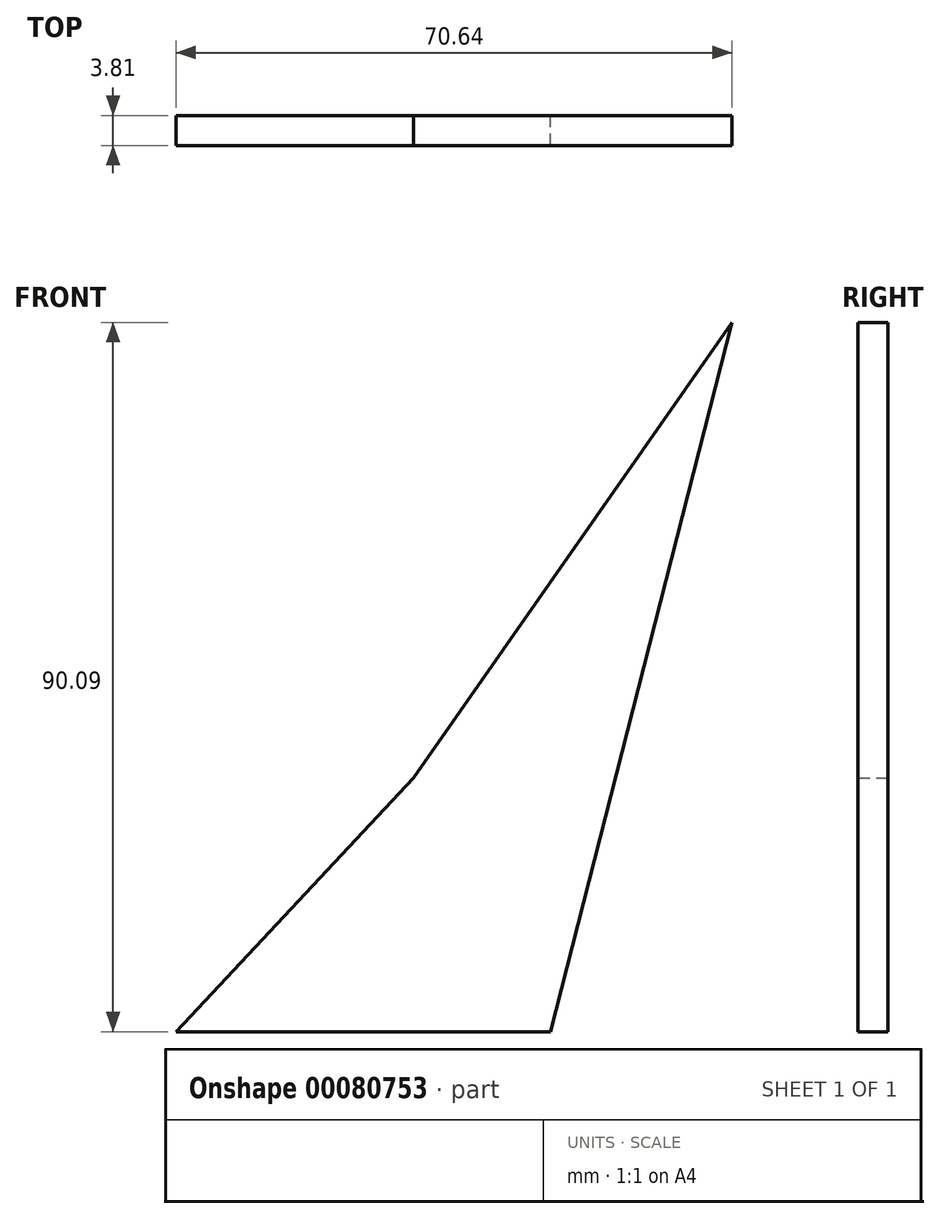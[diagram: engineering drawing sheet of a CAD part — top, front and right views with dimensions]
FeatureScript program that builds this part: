
annotation { "Feature Type Name" : "Feature", "Feature Type Description" : "" }
export const myFeature = defineFeature(function(context is Context, id is Id, definition is map)
    precondition{}
    {
        {
            var Q0;
            Q0=qCreatedBy(makeId("Front.planeOp"),FACE);
            var sketch = newSketch(context, id + "F0", { "sketchPlane" : qUnion([Q0])});
            skLineSegment(sketch, "E0", {"start": v(-18.04, 63.84) * mm, "end": v(-48.18, 31.62) * mm});
            skLineSegment(sketch, "E1", {"start": v(-48.18, 31.62) * mm, "end": v(-0.6, 31.62) * mm});
            skLineSegment(sketch, "E2", {"start": v(22.46, 121.71) * mm, "end": v(-0.6, 31.62) * mm});
            skLineSegment(sketch, "E3", {"start": v(-18.04, 63.84) * mm, "end": v(22.46, 121.71) * mm});
            skLineSegment(sketch, "E4", {"start": v(-0.6, 31.62) * mm, "end": v(-0.6, 121.71) * mm, "construction": true});
            skLineSegment(sketch, "E5", {"start": v(-0.6, 121.71) * mm, "end": v(22.46, 121.71) * mm, "construction": true});
            skSolve(sketch);
        }
        {
            var Q0;
            {var subQ1=sQuery(id+"F0.wireOp",EDGE,"rHa0fpeY-nUZA-mgX2-6ORY-aCar2YDQVBHJ");Q0=makeQuery(id+"F0.imprint","IMPRINT",FACE,{"disambiguationData":[TD([[makeQuery(id+"F0.imprint","IMPRINT",EDGE,{"derivedFrom":subQ1}),1.0]])]});}
            var Q1;
            {var subQ0=sQuery(id+"F0.wireOp",EDGE,"cS6nagYO-7f9N-Lp6B-XONn-p4yCG14qecv8");Q1=makeQuery(id+"F0.imprint","IMPRINT",FACE,{"disambiguationData":[TD([[makeQuery(id+"F0.imprint","IMPRINT",EDGE,{"derivedFrom":subQ0}),-1.0]])]});}
            var Q2;
            Q2=makeQuery(id+"F0.imprint","IMPRINT",FACE,{"disambiguationData":[TD([[makeQuery(id+"F0.imprint","IMPRINT",EDGE,{"derivedFrom":sQuery(id+"F0.wireOp",EDGE,"E0")}),1.0]])]});
            extrude(context, id + "F1", {"entities" : qUnion([Q0, Q1, Q2]), "depth" : 3.8 * mm});
        }
    });
